# Revit family: VCRD
name_source: partatom
category: Mechanical Equipment
units: mm (PartAtom-declared; Revit-internal decimal feet)

## family parameters
Always vertical = Yes
Cut with Voids When Loaded = No
Part Type = Normal
Room Calculation Point = No
Round Connector Dimension = Use Diameter
Shared = No
Work Plane-Based = No

## types (50) — shared parameters
1.5" = 1 1/2"
2" = 2"
Manufacturer = Loren Cook Company
ONE EIGTH = 1/8"
URL = www.lorencook.com
ZERO = 0"

## per-type parameters (varying)
| type | APLUSG | A_SUB | B_SUB | C_SUB | EIGHTH_T_SQ | ELEC | G_SUBDEPTH | HALF_B_SUB | INLET_HEIGHT | Model | RO/2 | ROOF_OPENING | T_SQ | T_SQ_HALF | Top_Rad | Type Comments | WB_RADIUS |
| 100_VCRD | 4 7/8" | 12 1/2" | 25 1/4" | 21 15/16" | 1 13/16" | 6 1/4" | 2" | 12 5/8" | 2 7/8" | VCRD | 6 3/4" | 13 1/2" | 18" | 9" | 3" | Upblast Centrifugal Exaust Ventilator Roof Mounted/Direct Drive | 4" |
| 120_VCRD | 3 13/16" | 19 1/16" | 30 3/16" | 28 1/4" | 2" | 9 17/32" | 2" | 15 3/32" | 1 13/16" | VCRD | 7 3/4" | 15 1/2" | 20" | 10" | 3" | Upblast Centrifugal Exaust Ventilator Roof Mounted/Direct Drive | 6" |
| 135_VCRD | 4 3/16" | 19 1/16" | 30 3/16" | 28 5/8" | 2" | 9 17/32" | 2" | 15 3/32" | 2 3/16" | VCRD | 7 3/4" | 15 1/2" | 20" | 10" | 3" | Upblast Centrifugal Exaust Ventilator Roof Mounted/Direct Drive | 6" |
| 150_VCRD | 5 1/16" | 20 15/16" | 34 11/16" | 30 1/4" | 2 13/32" | 10 15/32" | 2" | 17 11/32" | 3 1/16" | VCRD | 9 3/4" | 19 1/2" | 24" | 12" | 3" | Upblast Centrifugal Exaust Ventilator Roof Mounted/Direct Drive | 6" |
| 165_VCRD | 5 9/16" | 20 15/16" | 34 11/16" | 30 3/4" | 2 13/32" | 10 15/32" | 2" | 17 11/32" | 3 9/16" | VCRD | 9 3/4" | 19 1/2" | 24" | 12" | 3" | Upblast Centrifugal Exaust Ventilator Roof Mounted/Direct Drive | 6" |
| 180_VCRD | 6 15/16" | 24 13/16" | 39 7/16" | 35 7/8" | 3" | 12 13/32" | 3" | 19 23/32" | 3 15/16" | VCRD | 12 3/4" | 25 1/2" | 30" | 15" | 3" | Upblast Centrifugal Exaust Ventilator Roof Mounted/Direct Drive | 6" |
| 150_VCRD-HP | 5 1/16" | 20 15/16" | 34 11/16" | 27 1/2" | 2 13/32" | 10 15/32" | 2" | 17 11/32" | 3 1/16" | VCRD-HP | 9 3/4" | 19 1/2" | 24" | 12" | 3" | Upblast Centrifugal Exaust Ventilator Roof Mounted/Direct Drive | 6" |
| 165_VCRD-HP | 5 9/16" | 20 15/16" | 34 11/16" | 27 3/4" | 2 13/32" | 10 15/32" | 2" | 17 11/32" | 3 9/16" | VCRD-HP | 9 3/4" | 19 1/2" | 24" | 12" | 3" | Upblast Centrifugal Exaust Ventilator Roof Mounted/Direct Drive | 6" |
| 180_VCRD-HP | 6 15/16" | 24 13/16" | 39 7/16" | 33 3/8" | 3" | 12 13/32" | 3" | 19 23/32" | 3 15/16" | VCRD-HP | 12 3/4" | 25 1/2" | 30" | 15" | 3" | Upblast Centrifugal Exaust Ventilator Roof Mounted/Direct Drive | 6" |
| 195_VCD-HP | 7 7/16" | 24 13/16" | 39 7/16" | 33 1/2" | 3" | 12 13/32" | 3" | 19 23/32" | 4 7/16" | VCRD-HP | 12 3/4" | 25 1/2" | 30" | 15" | 3" | Upblast Centrifugal Exaust Ventilator Roof Mounted/Direct Drive | 7" |
| 165_VCRD-XP | 5 9/16" | 20 15/16" | 34 11/16" | 26 11/16" | 2 13/32" | 10 15/32" | 2" | 17 11/32" | 3 9/16" | VCRD-XP | 9 3/4" | 19 1/2" | 24" | 12" | 3" | Upblast Centrifugal Exaust Ventilator Roof Mounted/Direct Drive | 6" |
| 180_VCRD-XP | 6 15/16" | 24 13/16" | 39 7/16" | 31 9/16" | 3" | 12 13/32" | 3" | 19 23/32" | 3 15/16" | VCRD-XP | 12 3/4" | 25 1/2" | 30" | 15" | 3" | Upblast Centrifugal Exaust Ventilator Roof Mounted/Direct Drive | 6" |
| 195_VCRD-XP | 7 7/16" | 24 13/16" | 39 7/16" | 32 1/8" | 3" | 12 13/32" | 3" | 19 23/32" | 4 7/16" | VCRD-XP | 12 3/4" | 25 1/2" | 30" | 15" | 3" | Upblast Centrifugal Exaust Ventilator Roof Mounted/Direct Drive | 7" |
| 195_VCRD | 7 7/16" | 24 13/16" | 39 7/16" | 36 3/8" | 3" | 12 13/32" | 3" | 19 23/32" | 4 7/16" | VCRD | 12 3/4" | 25 1/2" | 30" | 15" | 3" | Upblast Centrifugal Exaust Ventilator Roof Mounted/Direct Drive | 7" |
| 210_VCRD | 7 7/16" | 25 15/16" | 45 1/4" | 38 3/8" | 3" | 12 31/32" | 3" | 22 5/8" | 4 7/16" | VCRD | 12 3/4" | 25 1/2" | 30" | 15" | 3" | Upblast Centrifugal Exaust Ventilator Roof Mounted/Direct Drive | 7" |
| 225_VCRD | 7 7/16" | 25 15/16" | 45 1/4" | 38 1/8" | 3" | 12 31/32" | 3" | 22 5/8" | 4 7/16" | VCRD | 12 3/4" | 25 1/2" | 30" | 15" | 3" | Upblast Centrifugal Exaust Ventilator Roof Mounted/Direct Drive | 7" |
| 245_VCRD | 7 7/16" | 28 1/2" | 49 1/4" | 41 1/16" | 3" | 14 1/4" | 3" | 24 5/8" | 4 7/16" | VCRD | 12 3/4" | 25 1/2" | 30" | 15" | 3" | Upblast Centrifugal Exaust Ventilator Roof Mounted/Direct Drive | 7" |
| 270_VCRD | 7 7/16" | 28 1/2" | 49 1/4" | 41 1/16" | 3 19/32" | 14 1/4" | 3" | 24 5/8" | 4 7/16" | VCRD | 15 3/4" | 31 1/2" | 36" | 18" | 3" | Upblast Centrifugal Exaust Ventilator Roof Mounted/Direct Drive | 7" |
| 300_VCRD | 7 7/16" | 33 7/8" | 54 1/4" | 49 15/16" | 3 19/32" | 16 15/16" | 3" | 27 1/8" | 4 7/16" | VCRD | 15 3/4" | 31 1/2" | 36" | 18" | 3" | Upblast Centrifugal Exaust Ventilator Roof Mounted/Direct Drive | 7" |
| 210_VCRD-HP | 7 7/16" | 25 15/16" | 45 1/4" | 35 3/8" | 3" | 12 31/32" | 3" | 22 5/8" | 4 7/16" | VCRD-HP | 12 3/4" | 25 1/2" | 30" | 15" | 3" | Upblast Centrifugal Exaust Ventilator Roof Mounted/Direct Drive | 7" |
| 210_VCRD-XP | 7 7/16" | 25 15/16" | 45 1/4" | 32 3/4" | 3" | 12 31/32" | 3" | 22 5/8" | 4 7/16" | VCRD-XP | 12 3/4" | 25 1/2" | 30" | 15" | 3" | Upblast Centrifugal Exaust Ventilator Roof Mounted/Direct Drive | 7" |
| 225_VCRD-HP | 7 7/16" | 25 15/16" | 45 1/4" | 33 5/16" | 3" | 12 31/32" | 3" | 22 5/8" | 4 7/16" | VCRD-HP | 12 3/4" | 25 1/2" | 30" | 15" | 3" | Upblast Centrifugal Exaust Ventilator Roof Mounted/Direct Drive | 7" |
| 225_VCRD-XP | 7 7/16" | 25 15/16" | 45 1/4" | 33 5/16" | 3" | 12 31/32" | 3" | 22 5/8" | 4 7/16" | VCRD-XP | 12 3/4" | 25 1/2" | 30" | 15" | 3" | Upblast Centrifugal Exaust Ventilator Roof Mounted/Direct Drive | 7" |
| 245_VCRD-HP | 7 7/16" | 28 1/2" | 49 1/4" | 37 5/16" | 3" | 14 1/4" | 3" | 24 5/8" | 4 7/16" | VCRD-HP | 12 3/4" | 25 1/2" | 30" | 15" | 3" | Upblast Centrifugal Exaust Ventilator Roof Mounted/Direct Drive | 7" |
| 245_VCRD-XP | 7 7/16" | 28 1/2" | 49 1/4" | 34 1/16" | 3" | 14 1/4" | 3" | 24 5/8" | 4 7/16" | VCRD-XP | 12 3/4" | 25 1/2" | 30" | 15" | 2" | Upblast Centrifugal Exaust Ventilator Roof Mounted/Direct Drive | 7" |
| 270_VCRD-HP | 7 7/16" | 28 1/2" | 49 1/4" | 37 5/16" | 3 19/32" | 14 1/4" | 3" | 24 5/8" | 4 7/16" | VCRD-HP | 15 3/4" | 31 1/2" | 36" | 18" | 3" | Upblast Centrifugal Exaust Ventilator Roof Mounted/Direct Drive | 7" |
| 270_VCRD-XP | 7 7/16" | 28 1/2" | 49 1/4" | 35" | 3 19/32" | 14 1/4" | 3" | 24 5/8" | 4 7/16" | VCRD-XP | 15 3/4" | 31 1/2" | 36" | 18" | 3" | Upblast Centrifugal Exaust Ventilator Roof Mounted/Direct Drive | 7" |
| 300_VCRD-HP | 7 7/16" | 33 7/8" | 54 1/4" | 45 15/16" | 3 19/32" | 16 15/16" | 3" | 27 1/8" | 4 7/16" | VCRD-HP | 15 3/4" | 31 1/2" | 36" | 18" | 3" | Upblast Centrifugal Exaust Ventilator Roof Mounted/Direct Drive | 7" |
| 300_VCRD-XP | 7 7/16" | 33 7/8" | 54 1/4" | 41 7/16" | 3 19/32" | 16 15/16" | 3" | 27 1/8" | 4 7/16" | VCRD-XP | 15 3/4" | 31 1/2" | 36" | 18" | 3" | Upblast Centrifugal Exaust Ventilator Roof Mounted/Direct Drive | 7" |
| 100_VCRD-VF | 4 7/8" | 12 1/2" | 25 1/4" | 22 5/16" | 1 13/16" | 6 1/4" | 2" | 12 5/8" | 2 7/8" | VCRD-VF | 6 3/4" | 13 1/2" | 18" | 9" | 3" | Upblast Centrifugal Exaust Ventilator Roof Mounted/Direct Drive Electronically Commutated Vari-Flow Motor | 4" |
| 120_VCRD-VF | 3 13/16" | 19 1/16" | 30 3/16" | 28 1/4" | 2" | 9 17/32" | 2" | 15 3/32" | 1 13/16" | VCRD-VF | 7 3/4" | 15 1/2" | 20" | 10" | 3" | Upblast Centrifugal Exaust Ventilator Roof Mounted/Direct Drive Electronically Commutated Vari-Flow Motor | 6" |
| 135_VCRD-VF | 4 3/16" | 19 1/16" | 30 3/16" | 28 5/8" | 2" | 9 17/32" | 2" | 15 3/32" | 2 3/16" | VCRD-VF | 7 3/4" | 15 1/2" | 20" | 10" | 3" | Upblast Centrifugal Exaust Ventilator Roof Mounted/Direct Drive Electronically Commutated Vari-Flow Motor | 6" |
| 150_VCRD-VF | 5 1/16" | 20 15/16" | 34 11/16" | 30 1/4" | 2 13/32" | 10 15/32" | 2" | 17 11/32" | 3 1/16" | VCRD-VF | 9 3/4" | 19 1/2" | 24" | 12" | 3" | Upblast Centrifugal Exaust Ventilator Roof Mounted/Direct Drive Electronically Commutated Vari-Flow Motor | 6" |
| 165_VCRD-VF | 5 9/16" | 20 15/16" | 34 11/16" | 30 3/4" | 2 13/32" | 10 15/32" | 2" | 17 11/32" | 3 9/16" | VCRD-VF | 9 3/4" | 19 1/2" | 24" | 12" | 3" | Upblast Centrifugal Exaust Ventilator Roof Mounted/Direct Drive Electronically Commutated Vari-Flow Motor | 6" |
| 180_VCRD-VF | 6 15/16" | 24 13/16" | 39 7/16" | 35 7/8" | 3" | 12 13/32" | 3" | 19 23/32" | 3 15/16" | VCRD-VF | 12 3/4" | 25 1/2" | 30" | 15" | 3" | Upblast Centrifugal Exaust Ventilator Roof Mounted/Direct Drive Electronically Commutated Vari-Flow Motor | 6" |
| 195_VCRD-VF | 7 7/16" | 24 13/16" | 39 7/16" | 36 3/8" | 3" | 12 13/32" | 3" | 19 23/32" | 4 7/16" | VCRD-VF | 12 3/4" | 25 1/2" | 30" | 15" | 3" | Upblast Centrifugal Exaust Ventilator Roof Mounted/Direct Drive Electronically Commutated Vari-Flow Motor | 7" |
| 210_VCRD-VF | 7 7/16" | 25 15/16" | 45 1/4" | 38 3/8" | 3" | 12 31/32" | 3" | 22 5/8" | 4 7/16" | VCRD-VF | 12 3/4" | 25 1/2" | 30" | 15" | 3" | Upblast Centrifugal Exaust Ventilator Roof Mounted/Direct Drive Electronically Commutated Vari-Flow Motor | 7" |
| 150_VCRD-HP-VF | 5 1/16" | 20 15/16" | 34 11/16" | 27 1/2" | 2 13/32" | 10 15/32" | 2" | 17 11/32" | 3 1/16" | VCRD-HP-VF | 9 3/4" | 19 1/2" | 24" | 12" | 3" | Upblast Centrifugal Exaust Ventilator Roof Mounted/Direct Drive Electronically Commutated Vari-Flow Motor | 6" |
| 165_VCRD-HP-VF | 5 9/16" | 20 15/16" | 34 11/16" | 27 3/4" | 2 13/32" | 10 15/32" | 2" | 17 11/32" | 3 9/16" | VCRD-HP-VF | 9 3/4" | 19 1/2" | 24" | 12" | 3" | Upblast Centrifugal Exaust Ventilator Roof Mounted/Direct Drive Electronically Commutated Vari-Flow Motor | 6" |
| 180_VCRD-HP-VF | 6 15/16" | 24 13/16" | 39 7/16" | 33 3/8" | 3" | 12 13/32" | 3" | 19 23/32" | 3 15/16" | VCRD-HP-VF | 12 3/4" | 25 1/2" | 30" | 15" | 3" | Upblast Centrifugal Exaust Ventilator Roof Mounted/Direct Drive Electronically Commutated Vari-Flow Motor | 6" |
| 195_VCRD-HP-VF | 7 7/16" | 24 13/16" | 39 7/16" | 33 1/2" | 3" | 12 13/32" | 3" | 19 23/32" | 4 7/16" | VCRD-HP-VF | 12 3/4" | 25 1/2" | 30" | 15" | 3" | Upblast Centrifugal Exaust Ventilator Roof Mounted/Direct Drive Electronically Commutated Vari-Flow Motor | 7" |
| 210_VCRD-HP-VF | 7 7/16" | 25 15/16" | 45 1/4" | 35 3/8" | 3" | 12 31/32" | 3" | 22 5/8" | 4 7/16" | VCRD-HP-VF | 12 3/4" | 25 1/2" | 30" | 15" | 3" | Upblast Centrifugal Exaust Ventilator Roof Mounted/Direct Drive Electronically Commutated Vari-Flow Motor | 7" |
| 165_VCRD-XP-VF | 5 9/16" | 20 15/16" | 34 11/16" | 26 11/16" | 2 13/32" | 10 15/32" | 2" | 17 11/32" | 3 9/16" | VCRD-XP-VF | 9 3/4" | 19 1/2" | 24" | 12" | 3" | Upblast Centrifugal Exaust Ventilator Roof Mounted/Direct Drive Electronically Commutated Vari-Flow Motor | 6" |
| 180_VCRD-XP-VF | 6 15/16" | 24 13/16" | 39 7/16" | 31 9/16" | 3" | 12 13/32" | 3" | 19 23/32" | 3 15/16" | VCRD-XP-VF | 12 3/4" | 25 1/2" | 30" | 15" | 3" | Upblast Centrifugal Exaust Ventilator Roof Mounted/Direct Drive Electronically Commutated Vari-Flow Motor | 6" |
| 195_VCRD-XP-VF | 7 7/16" | 24 13/16" | 39 7/16" | 32 1/8" | 3" | 12 13/32" | 3" | 19 23/32" | 4 7/16" | VCRD-XP-VF | 12 3/4" | 25 1/2" | 30" | 15" | 3" | Upblast Centrifugal Exaust Ventilator Roof Mounted/Direct Drive Electronically Commutated Vari-Flow Motor | 7" |
| 210_VCRD-XP-VF | 7 7/16" | 25 15/16" | 45 1/4" | 32 3/4" | 3" | 12 31/32" | 3" | 22 5/8" | 4 7/16" | VCRD-XP-VF | 12 3/4" | 25 1/2" | 30" | 15" | 3" | Upblast Centrifugal Exaust Ventilator Roof Mounted/Direct Drive Electronically Commutated Vari-Flow Motor | 7" |
| 225_VCRD-XP-VF | 7 7/16" | 25 15/16" | 45 1/4" | 33 5/16" | 3" | 12 31/32" | 3" | 22 5/8" | 4 7/16" | VCRD-XP-VF | 12 3/4" | 25 1/2" | 30" | 15" | 3" | Upblast Centrifugal Exaust Ventilator Roof Mounted/Direct Drive Electronically Commutated Vari-Flow Motor | 7" |
| 150_VCRD-EC | 5 1/16" | 20 15/16" | 34 11/16" | 30 1/4" | 2 13/32" | 10 15/32" | 2" | 17 11/32" | 3 1/16" | VCRD-EC | 9 3/4" | 19 1/2" | 24" | 12" | 3" | Upblast Centrifugal Exaust Ventilator Roof Mounted/Direct Drive with External Speed Control Electronically Commutated (EC) Motor Type N | 6" |
| 165_VCRD-HP-EC | 5 9/16" | 20 15/16" | 34 11/16" | 27 3/4" | 2 13/32" | 10 15/32" | 2" | 17 11/32" | 3 9/16" | VCRD-HP-EC | 9 3/4" | 19 1/2" | 24" | 12" | 3" | Upblast Centrifugal Exaust Ventilator Roof Mounted/Direct Drive with External Speed Control Electronically Commutated (EC) Motor Type N | 6" |
| 195_VCRD-XP-EC | 7 7/16" | 24 13/16" | 39 7/16" | 32 1/8" | 3" | 12 13/32" | 3" | 19 23/32" | 4 7/16" | VCRD-XP-EC | 12 3/4" | 25 1/2" | 30" | 15" | 3" | Upblast Centrifugal Exaust Ventilator Roof Mounted/Direct Drive with External Speed Control Electronically Commutated (EC) Motor Type N | 7" |

## geometry (parser evidence)
native form markers: Sweep x2
no freeform markers — native parametric forms only
